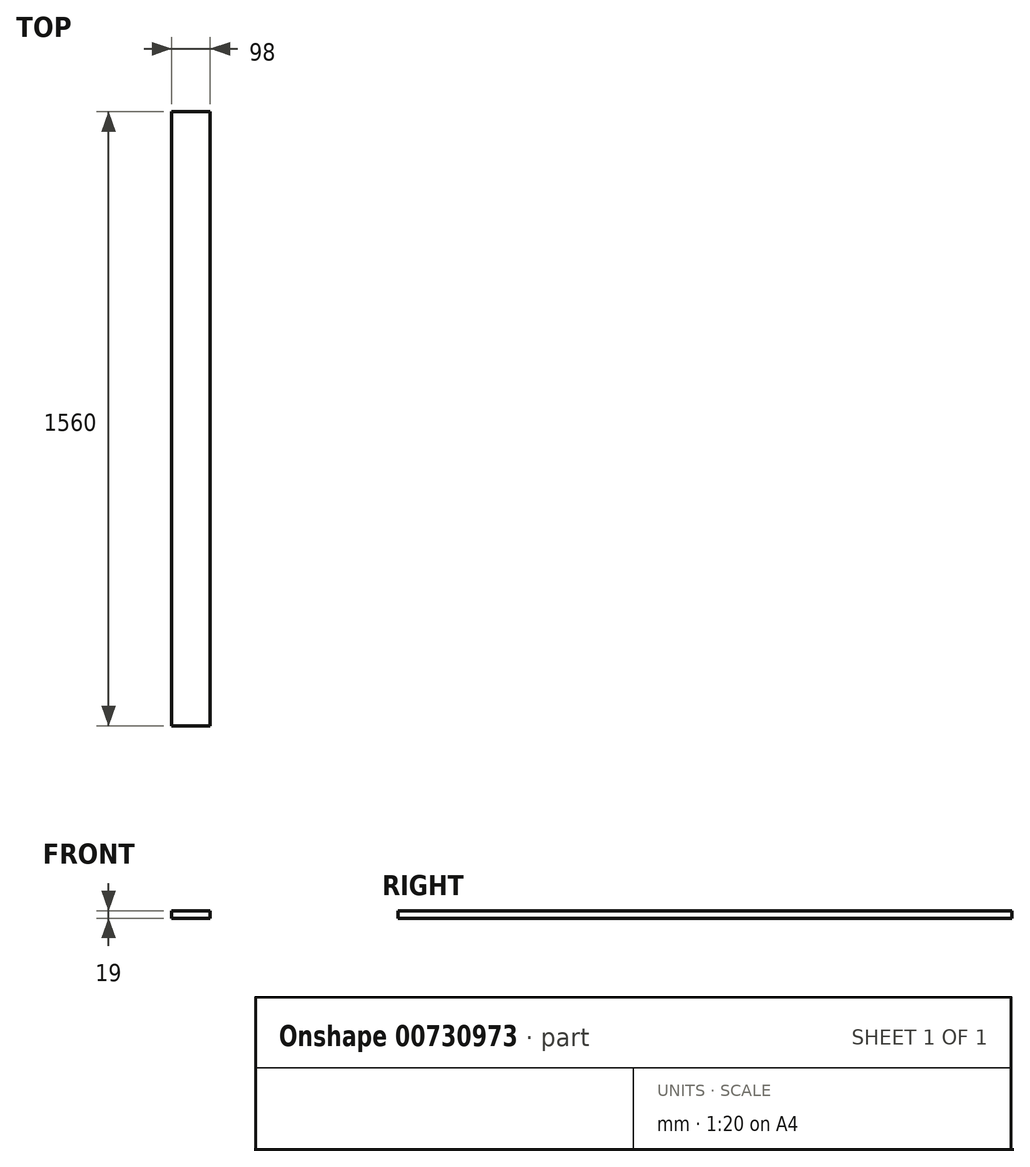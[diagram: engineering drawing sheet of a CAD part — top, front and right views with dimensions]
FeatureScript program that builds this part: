
annotation { "Feature Type Name" : "Feature", "Feature Type Description" : "" }
export const myFeature = defineFeature(function(context is Context, id is Id, definition is map)
    precondition{}
    {
        {
            var Q0;
            Q0=qCreatedBy(makeId("Front.planeOp"),FACE);
            var sketch = newSketch(context, id + "F0", { "sketchPlane" : qUnion([Q0])});
            skLineSegment(sketch, "E0.bottom", {"start": v(49, -9.5) * mm, "end": v(-49, -9.5) * mm});
            skLineSegment(sketch, "E0.top", {"start": v(49, 9.5) * mm, "end": v(-49, 9.5) * mm});
            skLineSegment(sketch, "E0.left", {"start": v(49, -9.5) * mm, "end": v(49, 9.5) * mm});
            skLineSegment(sketch, "E0.right", {"start": v(-49, -9.5) * mm, "end": v(-49, 9.5) * mm});
            skPoint(sketch, "E0.middle", {"position": v(0, 0) * mm});
            skSolve(sketch);
        }
        {
            var Q0;
            Q0=makeQuery(id+"F0.imprint","IMPRINT",FACE,{"disambiguationData":[TD([[makeQuery(id+"F0.imprint","IMPRINT",EDGE,{"derivedFrom":sQuery(id+"F0.wireOp",EDGE,"E0.bottom")}),-1.0]])]});
            extrude(context, id + "F1", {"entities" : qUnion([Q0]), "depth" : 1560 * mm, "offsetDistance" : 25 * mm});
        }
    });
